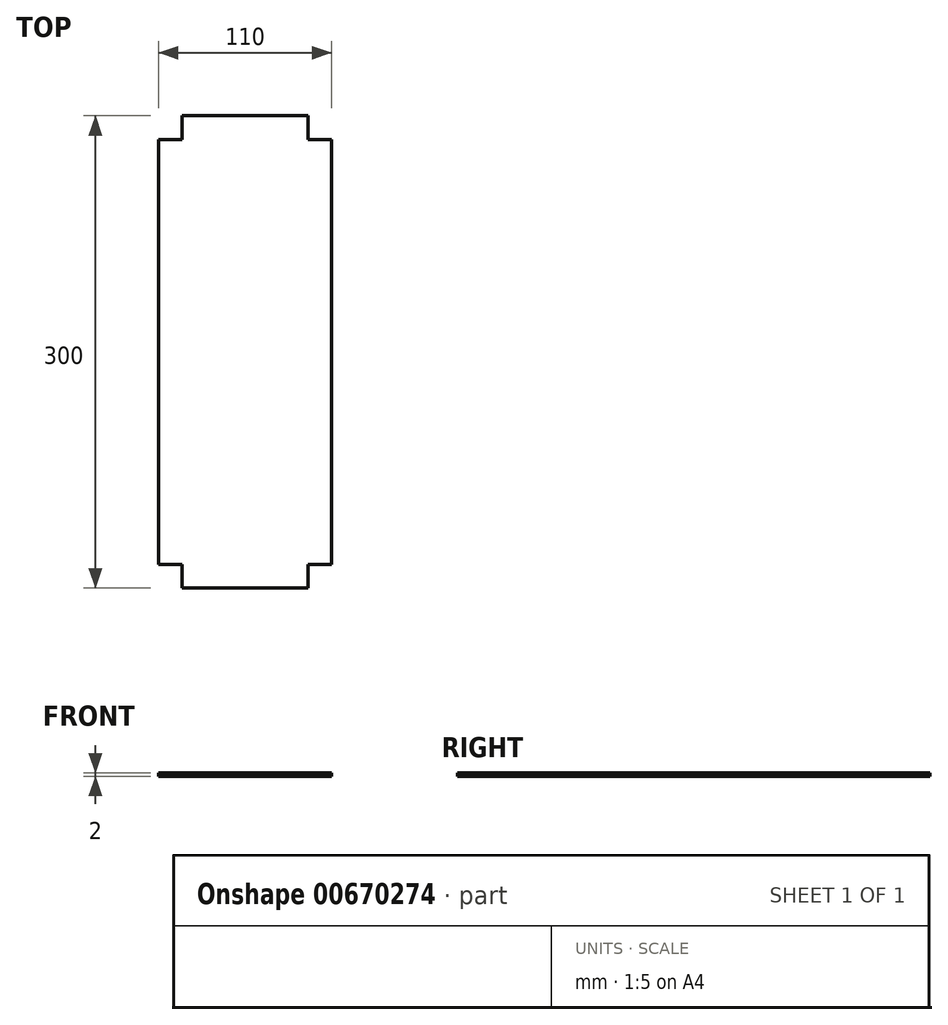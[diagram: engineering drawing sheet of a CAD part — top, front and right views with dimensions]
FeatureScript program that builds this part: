
annotation { "Feature Type Name" : "Feature", "Feature Type Description" : "" }
export const myFeature = defineFeature(function(context is Context, id is Id, definition is map)
    precondition{}
    {
        {
            var Q0;
            Q0=qCreatedBy(makeId("Top.planeOp"),FACE);
            var sketch = newSketch(context, id + "F0", { "sketchPlane" : qUnion([Q0])});
            skLineSegment(sketch, "E0.bottom", {"start": v(-32.49, 247.74) * mm, "end": v(47.51, 247.74) * mm});
            skLineSegment(sketch, "E0.top", {"start": v(-32.49, -52.26) * mm, "end": v(47.51, -52.26) * mm});
            skLineSegment(sketch, "E0.left", {"start": v(-32.49, 247.74) * mm, "end": v(-32.49, -52.26) * mm});
            skLineSegment(sketch, "E0.right", {"start": v(47.51, 247.74) * mm, "end": v(47.51, -52.26) * mm});
            skLineSegment(sketch, "E1", {"start": v(47.51, 232.74) * mm, "end": v(62.51, 232.74) * mm});
            skLineSegment(sketch, "E2", {"start": v(62.51, 232.74) * mm, "end": v(62.51, -37.26) * mm});
            skLineSegment(sketch, "E3", {"start": v(62.51, -37.26) * mm, "end": v(47.51, -37.26) * mm});
            skLineSegment(sketch, "E4", {"start": v(-32.49, 232.74) * mm, "end": v(-47.49, 232.74) * mm});
            skLineSegment(sketch, "E5", {"start": v(-47.49, 232.74) * mm, "end": v(-47.49, -37.26) * mm});
            skLineSegment(sketch, "E6", {"start": v(-47.49, -37.26) * mm, "end": v(-32.49, -37.26) * mm});
            skSolve(sketch);
        }
        {
            var Q0;
            {var subQ3=sQuery(id+"F0.wireOp",EDGE,"E0.bottom");Q0=makeQuery(id+"F0.imprint","IMPRINT",FACE,{"disambiguationData":[TD([[makeQuery(id+"F0.imprint","IMPRINT",EDGE,{"derivedFrom":subQ3}),-1.0]])]});}
            var Q1;
            {var subQ0=sQuery(id+"F0.wireOp",EDGE,"E4");Q1=makeQuery(id+"F0.imprint","IMPRINT",FACE,{"disambiguationData":[TD([[makeQuery(id+"F0.imprint","IMPRINT",EDGE,{"derivedFrom":subQ0}),1.0]])]});}
            var Q2;
            {var subQ0=sQuery(id+"F0.wireOp",EDGE,"E1");Q2=makeQuery(id+"F0.imprint","IMPRINT",FACE,{"disambiguationData":[TD([[makeQuery(id+"F0.imprint","IMPRINT",EDGE,{"derivedFrom":subQ0}),-1.0]])]});}
            extrude(context, id + "F1", {"entities" : qUnion([Q0, Q1, Q2]), "depth" : 2 * mm, "offsetDistance" : 25 * mm});
        }
    });
